# Revit family: 3034787 Sylvania Lighting Fixture GIOTTO305 LED G2 3000K RECESSED 1-10V EMERGENCY
name_source: partatom
category: Lighting Fixtures
revit_build: Autodesk Revit 2016 (Build: 20150220_1215(x64)
units: mm (PartAtom-declared; Revit-internal decimal feet)

## family parameters
Cut with Voids When Loaded = No
Host = Face
Light Source = Yes
OmniClass Number = 23.80.70.00
OmniClass Title = Lighting
Part Type = Normal
Room Calculation Point = No
Round Connector Dimension = Use Diameter
Shared = No

## types (2) — shared parameters
Apparent Load = 20 VA
Assembly Code = D5020200
AssetType = Fixed
ClassificationName = Uniclass2015
ClassificationValue = EF_70_80
Color Filter = 16777215
Default Elevation = 1219 mm
Description = Ambient and decorative round, recessed mounted LED bulkhead luminaire. White robust polycarbonate body with opal diffuser, 1490 lm, 20W, 75lm/W, 3000K, CRI 80, 1-10V dimmable, integral 3 hour maintained emergency, 50,000 hours lumen maintenance. Drive current: 700mA, IP44, IK10, Class I, 220-240V, Energy class: A++, A+, A.
Diameter_SYL = 305 mm  [stored 1.00066 ft]
DiffuserRadius_SYL = 283 mm
Dimming Lamp Color Temperature Shift = <None>
DocumentationLiterature = http://www.sylvania-lighting.com
DurationUnit = hours
ElectricShockClassification = Class I
Emit Shape Visible in Rendering = No
Emit from Circle Diameter = 317 mm  [stored 1.04003 ft]
ExpectedLife = 50000
Height_SYL = 104 mm
IfcExportAs = IfcLightFixtureType
IfcExportType = IfcLightFixtureType
ImpactProtectionIndex = IK10
IngressProtection = IP44
Keynote = 16500
Lamp = LED
LampColourRenderingIndex = 80
LampColourTemperature = 3000 K
LampsType = LED
Manufacturer = Feilo Sylvania
ManufacturerName = Feilo Sylvania
Material = polycarbonate housing, polycarbonate diffuser
Material_1_SYL = Polycarbonate_Sylvania_Giotto_White
Material_2_SYL = Polycarbonate_Sylvania_Giotto_Opal
Material_3_SYL = LED-Sylvania
Material_4_SYL = <By Category>
ModelNumber = 3034787
NominalDepth = 305 mm  [stored 1.00066 ft]
NominalHeight = 104 mm
NominalLength = 305 mm  [stored 1.00066 ft]
PowerConsumption = 20 W
Tilt Angle = -90.00°
Type Image = <None>
URL = http://www.sylvania-lighting.com
Voltage = 0 V
Weight = 1.41 kg
zero-valued in all types: Cost, PowerFactor

## per-type parameters (varying)
| type | LampNominalLuminous | LuminousEfficacy | Model | ModelReference | Name | Photometric Web File | TypeName |
| 3034787 GIOTTO305 LED G2 3000K RECESSED 1-10V EMERGENCY Emergency mode | 109 lm | 5.45 lm/W | GIOTTO305 LED G2 3000K RECESSED 1-10V EMERGENCY Emergency mode | GIOTTO305 LED G2 3000K RECESSED 1-10V EMERGENCY Emergency mode | GIOTTO305 LED G2 3000K RECESSED 1-10V EMERGENCY Emergency mode | 3034787EM.ies | GIOTTO305 LED G2 3000K RECESSED 1-10V EMERGENCY Emergency mode |
| 3034787 GIOTTO305 LED G2 3000K RECESSED 1-10V EMERGENCY | 1490 lm | 75 lm/W | GIOTTO305 LED G2 3000K RECESSED 1-10V EMERGENCY | GIOTTO305 LED G2 3000K RECESSED 1-10V EMERGENCY | GIOTTO305 LED G2 3000K RECESSED 1-10V EMERGENCY | 3034787.ies | GIOTTO305 LED G2 3000K RECESSED 1-10V EMERGENCY |

note: [stored X ft] marks values corroborated as IEEE doubles in the binary element streams (Revit-internal decimal feet)

## geometry (parser evidence)
native form markers: Sweep x3
no freeform markers — native parametric forms only
